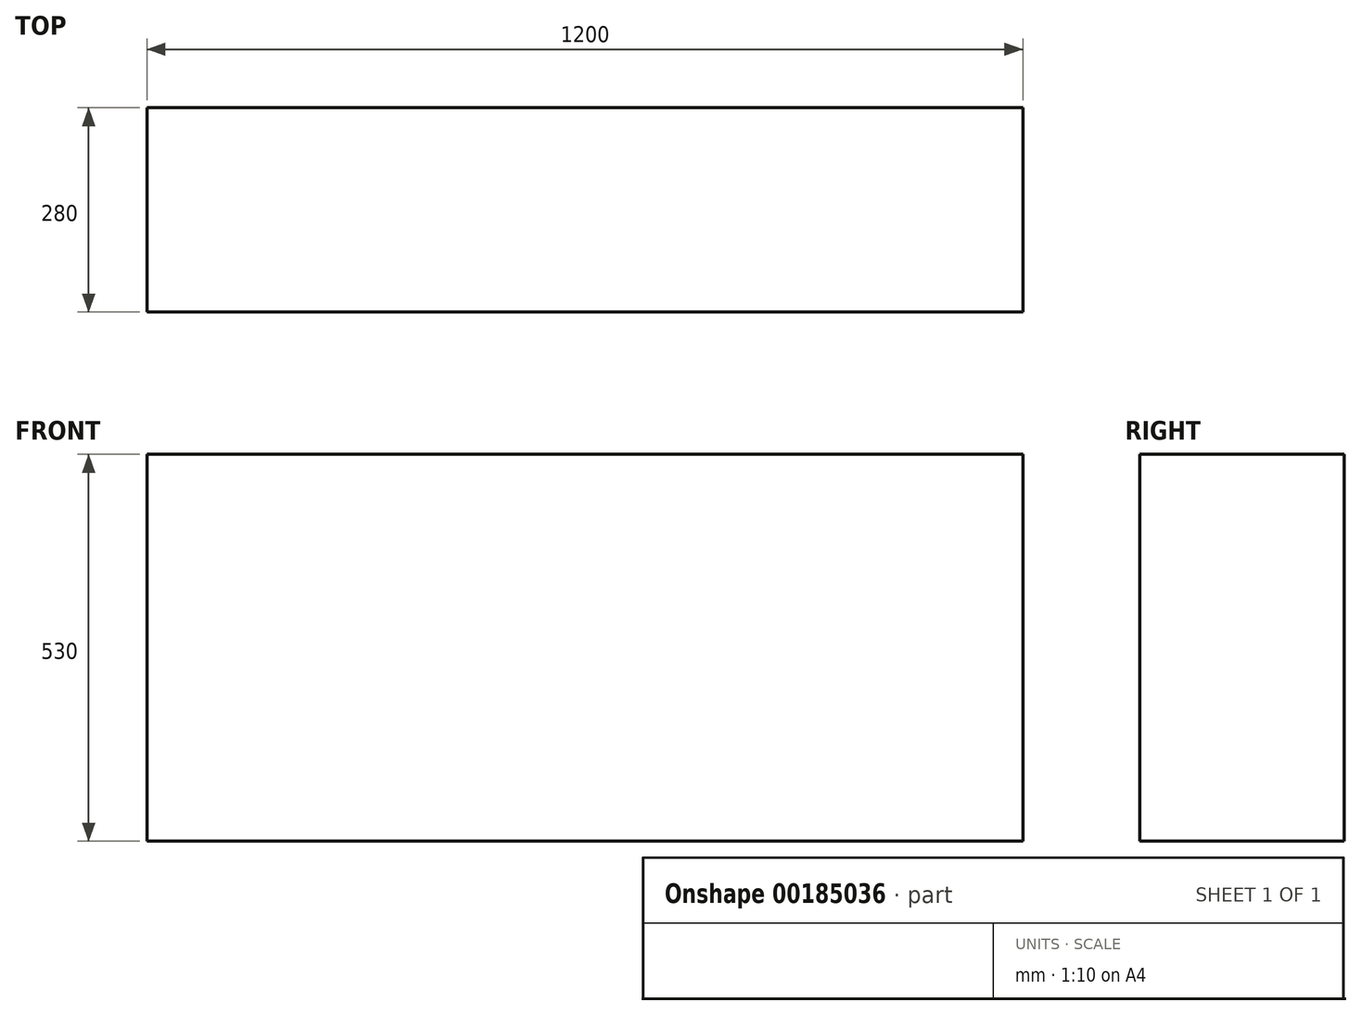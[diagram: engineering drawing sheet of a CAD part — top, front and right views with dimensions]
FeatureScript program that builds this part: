
annotation { "Feature Type Name" : "Feature", "Feature Type Description" : "" }
export const myFeature = defineFeature(function(context is Context, id is Id, definition is map)
    precondition{}
    {
        {
            var Q0;
            Q0=qCreatedBy(makeId("Top.planeOp"),FACE);
            var sketch = newSketch(context, id + "F0", { "sketchPlane" : qUnion([Q0])});
            skLineSegment(sketch, "E0", {"start": v(-596.98, -301.74) * mm, "end": v(-596.98, -581.74) * mm});
            skLineSegment(sketch, "E1", {"start": v(-596.98, -581.74) * mm, "end": v(603.02, -581.74) * mm});
            skLineSegment(sketch, "E2", {"start": v(603.02, -581.74) * mm, "end": v(603.02, -301.74) * mm});
            skLineSegment(sketch, "E3", {"start": v(603.02, -301.74) * mm, "end": v(-596.98, -301.74) * mm});
            skSolve(sketch);
        }
        {
            var Q0;
            Q0 = qSketchRegion(id + "F0", true);
            extrude(context, id + "F1", {"entities" : qUnion([Q0]), "flatOperationType" : FlatOperationType.REMOVE, "offsetDistance" : 25 * mm, "depth" : 530 * mm, "domain" : OperationDomain.MODEL});
        }
    });
